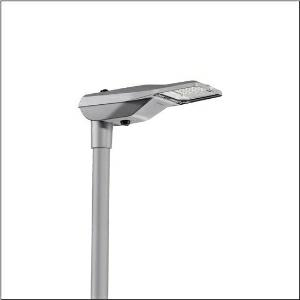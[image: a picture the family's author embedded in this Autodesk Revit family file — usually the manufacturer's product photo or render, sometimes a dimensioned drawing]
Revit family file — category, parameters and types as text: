
# Revit family: streetlight_sl_21_iq_micro___stw1_0a_5xe1e31y08cb_f1b3
name_source: partatom
category: Lighting Fixtures
units: mm (PartAtom-declared; Revit-internal decimal feet)

## family parameters
Cut with Voids When Loaded = No
Host = Face
Light Source = No
Part Type = Normal
Room Calculation Point = No
Round Connector Dimension = Use Diameter
Shared = No

## types (1)
- --- (1 x LED, 2880 lm, 19.1 W, 3000K)
    Apparent Load = 19 VA
    CIE Flux Codes = 38 75 98 100 100
    Color Rendering = 70
    Color Temperature = 3000K
    Default Elevation = 1800 mm
    Description = Streetlight SL 21 iQ micro, mast luminaire, primary light control with lens, of PMMA, primary optical cover: cover, of toughened safety glass, transparent, light distribution: STW1.0a, light emission: direct distribution, primary light characteristic: asymmetric, installation type: post-top, side-entry, LED, High Power LED, rated luminous flux: 2.880lm, luminous efficacy: 151lm/W, light colour: 730, colour temperature: 3000K, control gear: iQ-Street Remote, D4i with power reduction, control: pre-setting: logarithmic dimming characteristic, Street-Remote, Auto-Match, Temp-Guard, Lumen-Switch, Night-Set, Smart-Wire, Light-Fading, Desk-Remote (wireless, voltage-free reading and setting of iQ features in the workshop via application-optimized NFC function/RFID function), optimised constant luminous flux control (CLO 2.0), mains connection: 220..240V, AC, 50/60Hz, start of lifetime: 19W, end of service life: 20W, reduction: 9W, luminaire housing, of diecast aluminium, powder-coated, Siteco® metallic grey (DB 702S), corrosivity category C5 mid according to DIN EN ISO 12944, please order mast flange separately, inclination adjustable: 0°, 5°, 10°, 15°, sealing non-destructively replaceable, multi-level sealing system, length: 528mm, width: 235mm, height: 110mm, mast flange for spigot size: 42mm (side-entry): 5XC10008XM4, 60/48mm (side-entry/post-top): 5XC10108XM2, 76/60mm (side-entry/post-top): 5XC10108XM1, mounting height: 4..8m, Smart Interface below and above, protection rating (complete): IP66, insulation class (complete): insulation class II (safety insulation), certification: CE, ENEC, ENEC+, VDE, impact resistance: IK10, permissible operating ambient temperature for outdoor applications: -40..+50°C, standard-compliant lighting for roads and squares, packaging unit: 1 piece

Light Distribution: STW1.0a
    Height = 110 mm
    Lamp = 1 x LED
    Lamp Light Flux = 2880 lm
    Lamp Power = 19.1 W
    Lamp count = 1
    Length = 528 mm
    Luminous efficacy = 151 lm/W
    Manufacturer = Siteco
    ModVariant = No
    Model = 5XE1E31Y08CB
    Number of Poles = 1
    OnlyDefault = Yes
    Power Factor = 1
    Product Name = Streetlight SL 21 iQ micro | STW1.0a
    Product group = mast luminaire | pylon top
    ProductGroupID = 6100
    Protection Class = Protection class II
    Protection Degree = IP 66
    RLX_Detail_Level = 1
    RLX_Emergency_Light_Flux = 0 lm
    RLX_Emergency_Type = 0
    RLX_Emergency_Type_DB = No
    RlxData = <blob elided: 99153 chars, md5=69f4dff4>
    Socket = socket
    Standby Power = 0 W
    System Light Flux = 2880 lm
    System Power = 19 W
    Type Comments = factory setting: luminous flux: 100 % | dim-lin: 254 | 387 mA
    Type Image = l_1007239.jpg
    URL = http://relux.com
    VarID = @adj_114416
    Voltage = 0 V
    Weight = 0.00 kg
    Width = 235 mm

## geometry (parser evidence)
native form markers: Blend x4, Sweep x8
no freeform markers — native parametric forms only
